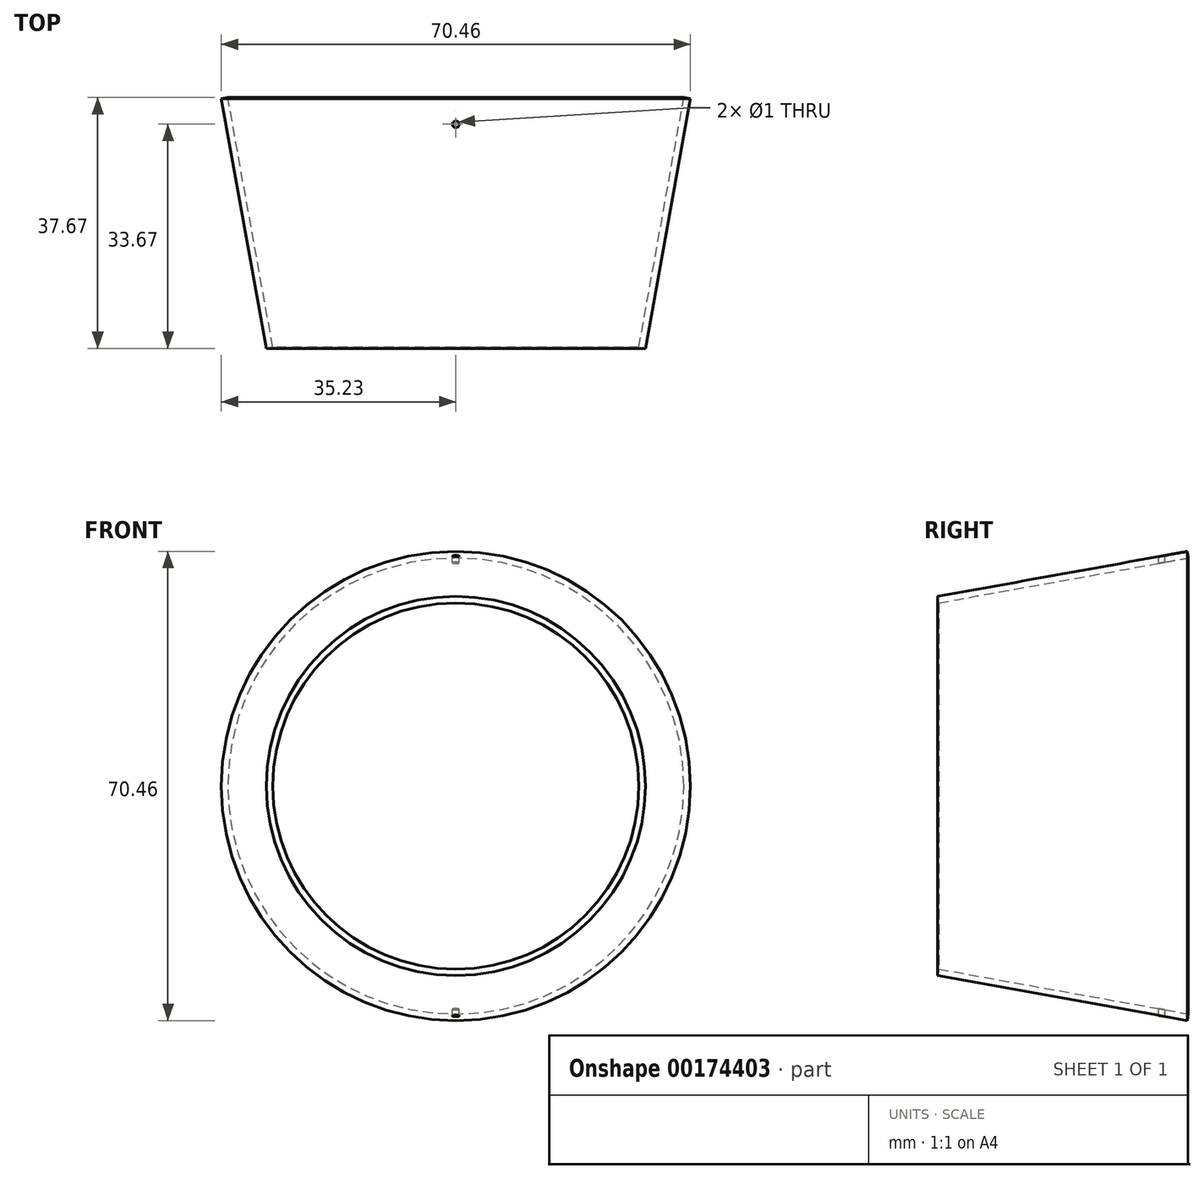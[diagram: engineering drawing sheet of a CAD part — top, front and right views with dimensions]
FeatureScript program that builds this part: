
annotation { "Feature Type Name" : "Feature", "Feature Type Description" : "" }
export const myFeature = defineFeature(function(context is Context, id is Id, definition is map)
    precondition{}
    {
        {
            var Q0;
            Q0=qCreatedBy(makeId("Right.planeOp"),FACE);
            var sketch = newSketch(context, id + "F0", { "sketchPlane" : qUnion([Q0])});
            skLineSegment(sketch, "E0", {"start": v(4, 34.25) * mm, "end": v(-33.5, 27.5) * mm});
            skLineSegment(sketch, "E1", {"start": v(-33.5, 27.5) * mm, "end": v(-33.67, 28.48) * mm});
            skLineSegment(sketch, "E2", {"start": v(-33.67, 28.48) * mm, "end": v(3.82, 35.23) * mm});
            skLineSegment(sketch, "E3", {"start": v(3.82, 35.23) * mm, "end": v(4, 34.25) * mm});
            skLineSegment(sketch, "E4", {"start": v(-5.85, 32.48) * mm, "end": v(0, 0) * mm, "construction": true});
            skLineSegment(sketch, "E5", {"start": v(-33.5, 27.5) * mm, "end": v(-33.5, 0) * mm, "construction": true});
            skLineSegment(sketch, "E6", {"start": v(4, 34.25) * mm, "end": v(4, 0) * mm, "construction": true});
            skLineSegment(sketch, "E7", {"start": v(4, 0) * mm, "end": v(0, 0) * mm, "construction": true});
            skSolve(sketch);
        }
        {
            var Q0;
            Q0 = qSketchRegion(id + "F0", true);
            var Q1;
            Q1=sQuery(id+"F0.wireOp",EDGE,"E7");
            revolve(context, id + "F1", {"entities" : qUnion([Q0]), "axis" : qUnion([Q1]), "revolveType" : RevolveType.FULL});
        }
        {
            var Q0;
            Q0=qCreatedBy(makeId("Top.planeOp"),FACE);
            var sketch = newSketch(context, id + "F2", { "sketchPlane" : qUnion([Q0])});
            skCircle(sketch, "E8", {"center": v(0, 0) * mm, "radius": 0.5 * mm});
            skSolve(sketch);
        }
        {
            var Q0;
            Q0 = qSketchRegion(id + "F2", true);
            extrude(context, id + "F3", {"entities" : qUnion([Q0]), "operationType" : NewBodyOperationType.REMOVE, "endBound" : BoundingType.THROUGH_ALL, "oppositeDirection" : true, "depth" : 25 * mm, "hasSecondDirection" : true, "secondDirectionBound" : SecondDirectionBoundingType.THROUGH_ALL, "secondDirectionOppositeDirection" : false, "secondDirectionDepth" : 25 * mm});
        }
    });
